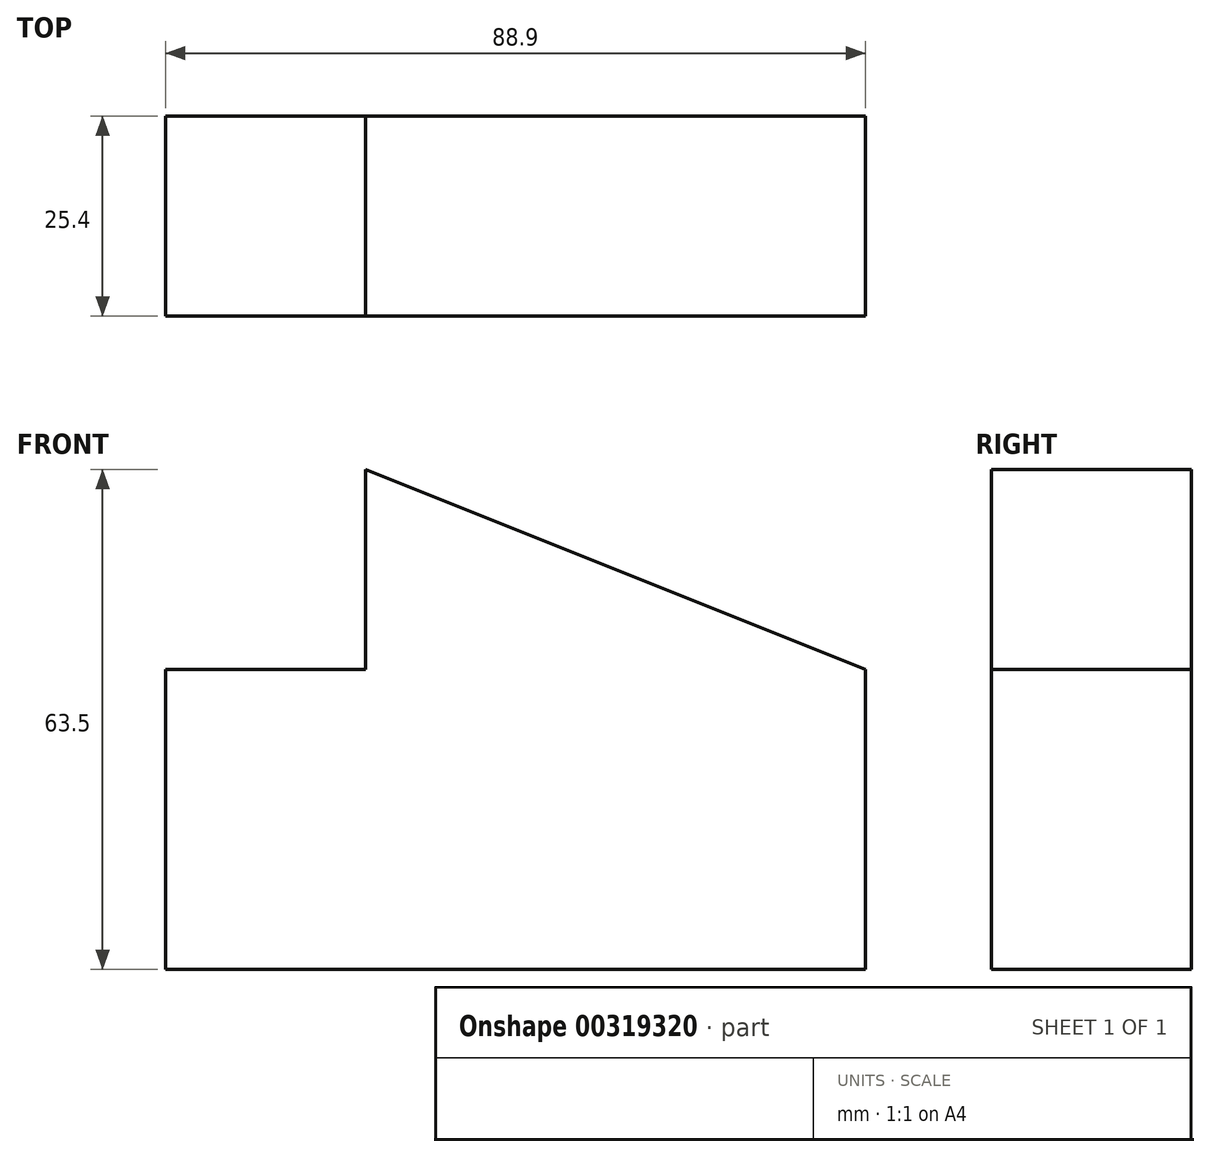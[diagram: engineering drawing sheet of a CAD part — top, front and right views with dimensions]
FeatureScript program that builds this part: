
annotation { "Feature Type Name" : "Feature", "Feature Type Description" : "" }
export const myFeature = defineFeature(function(context is Context, id is Id, definition is map)
    precondition{}
    {
        {
            var Q0;
            Q0=qCreatedBy(makeId("Front.planeOp"),FACE);
            var sketch = newSketch(context, id + "F0", { "sketchPlane" : qUnion([Q0])});
            skLineSegment(sketch, "E0", {"start": v(-50.93, -45.14) * mm, "end": v(37.97, -45.14) * mm});
            skLineSegment(sketch, "E1", {"start": v(37.97, -45.14) * mm, "end": v(37.97, -7.04) * mm});
            skLineSegment(sketch, "E2", {"start": v(-50.93, -45.14) * mm, "end": v(-50.93, -7.04) * mm});
            skLineSegment(sketch, "E3", {"start": v(-50.93, -7.04) * mm, "end": v(-25.53, -7.04) * mm});
            skLineSegment(sketch, "E4", {"start": v(-25.53, -7.04) * mm, "end": v(-25.53, 18.36) * mm});
            skLineSegment(sketch, "E5", {"start": v(-25.53, 18.36) * mm, "end": v(37.97, -7.04) * mm});
            skSolve(sketch);
        }
        {
            var Q0;
            Q0 = qSketchRegion(id + "F0", true);
            var Q1;
            Q1=makeQuery(id+"F0.imprint","IMPRINT",FACE,{"disambiguationData":[TD([[makeQuery(id+"F0.imprint","IMPRINT",EDGE,{"derivedFrom":sQuery(id+"F0.wireOp",EDGE,"E0")}),1.0]])]});
            extrude(context, id + "F1", {"entities" : qUnion([Q0, Q1]), "depth" : 25.4 * mm});
        }
    });
